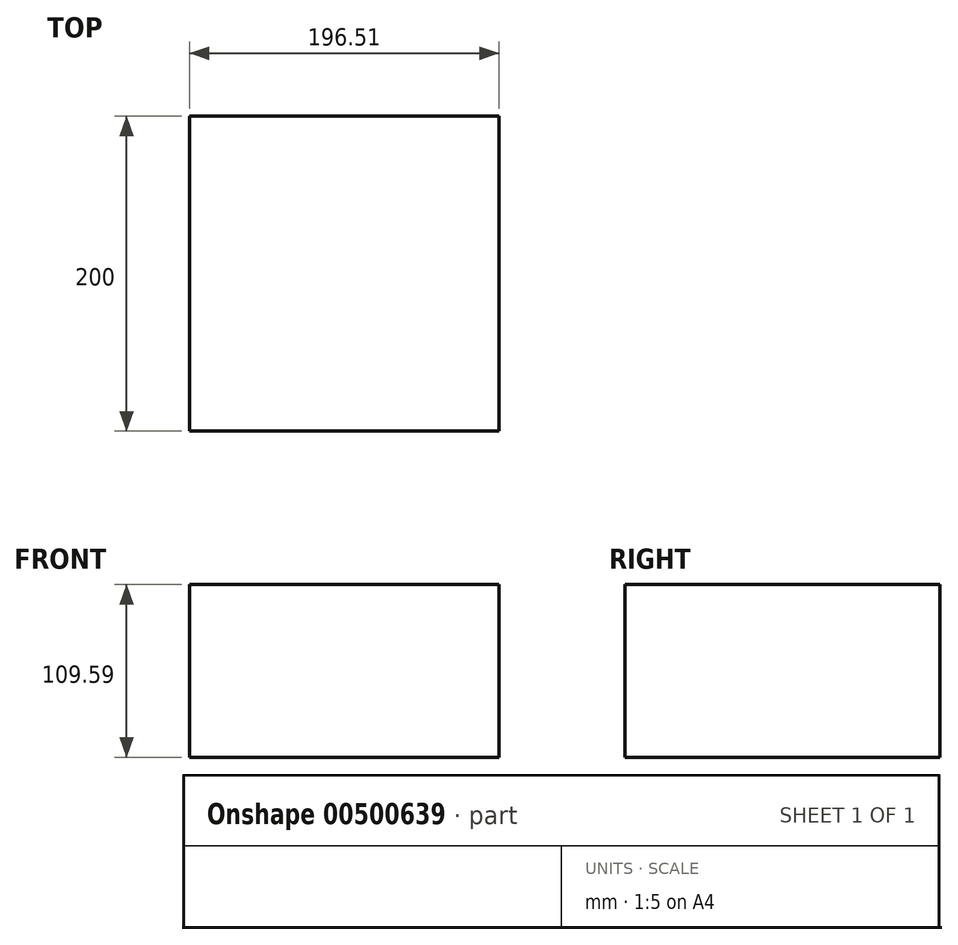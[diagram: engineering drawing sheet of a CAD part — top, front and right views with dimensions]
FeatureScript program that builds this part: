
annotation { "Feature Type Name" : "Feature", "Feature Type Description" : "" }
export const myFeature = defineFeature(function(context is Context, id is Id, definition is map)
    precondition{}
    {
        {
            var Q0;
            Q0=qCreatedBy(makeId("Front.planeOp"),FACE);
            var sketch = newSketch(context, id + "F0", { "sketchPlane" : qUnion([Q0])});
            skLineSegment(sketch, "E0.bottom", {"start": v(-98.4, -54.65) * mm, "end": v(98.11, -54.65) * mm});
            skLineSegment(sketch, "E0.top", {"start": v(-98.4, 54.94) * mm, "end": v(98.11, 54.94) * mm});
            skLineSegment(sketch, "E0.left", {"start": v(-98.4, -54.65) * mm, "end": v(-98.4, 54.94) * mm});
            skLineSegment(sketch, "E0.right", {"start": v(98.11, -54.65) * mm, "end": v(98.11, 54.94) * mm});
            skSolve(sketch);
        }
        {
            var Q0;
            Q0=makeQuery(id+"F0.imprint","IMPRINT",FACE,{"disambiguationData":[TD([[makeQuery(id+"F0.imprint","IMPRINT",EDGE,{"derivedFrom":sQuery(id+"F0.wireOp",EDGE,"E0.bottom")}),1.0]])]});
            extrude(context, id + "F1", {"entities" : qUnion([Q0]), "depth" : 200 * mm});
        }
    });
